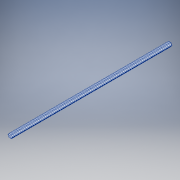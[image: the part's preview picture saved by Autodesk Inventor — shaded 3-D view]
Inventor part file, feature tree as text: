
AUTODESK INVENTOR PART (.ipt)
format: ipt  version: 2017 (Build 210142000, 142)  size: 183,808 bytes
history: native  units: in
note: dims shown in document units (in); Inventor stores cm internally (conversion verified against a paired STEP export)
features: extrude x2, sketch x2, projected_geometry x2, other x1
ambient origin geometry x8: Origin, YZ Plane, XZ Plane, XY Plane, X Axis, Y Axis, Z Axis, Center Point
bodies: Solid1 (feature_tree)
feature tree (7):
  other  "Boss-Extrude1"
  extrude  "Extrusion1"  Depth=21.25in TaperAngle=0.0deg
  extrude  "Extrusion2"  [1 undecoded]
  sketch  "Sketch1"  dims[d0=21.25in d1=0.0in d2=9.25in d3=0.0in]
  projected_geometry  "Projected Loop1"
  sketch  "Sketch4"
  projected_geometry  "Projected Loop2"
note: 1 required parameter value undecoded (feature->parameter linkage not recoverable at this tier; creation-order binding heuristic only, values carry confidence <= 0.55)
